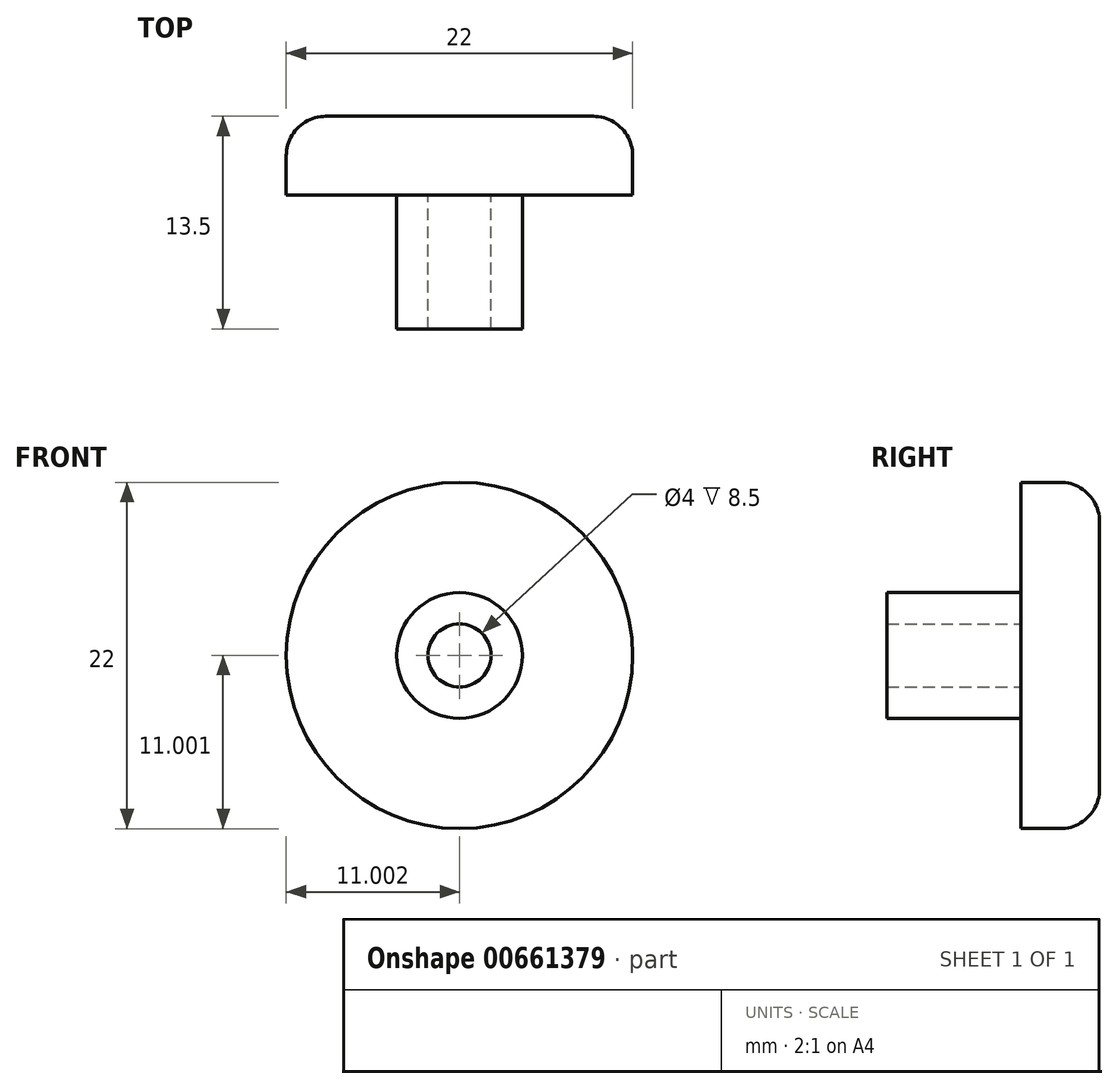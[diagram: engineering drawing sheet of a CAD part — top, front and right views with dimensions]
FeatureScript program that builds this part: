
annotation { "Feature Type Name" : "Feature", "Feature Type Description" : "" }
export const myFeature = defineFeature(function(context is Context, id is Id, definition is map)
    precondition{}
    {
        {
            var Q0;
            Q0=qCreatedBy(makeId("Front.planeOp"),FACE);
            var sketch = newSketch(context, id + "F0", { "sketchPlane" : qUnion([Q0])});
            skCircle(sketch, "E0", {"center": v(39.71, 36.2) * mm, "radius": 11 * mm});
            skCircle(sketch, "E1", {"center": v(39.71, 36.2) * mm, "radius": 4 * mm});
            skCircle(sketch, "E2", {"center": v(39.71, 36.2) * mm, "radius": 2 * mm});
            skSolve(sketch);
        }
        {
            var Q0;
            Q0=makeQuery(id+"F0.imprint","IMPRINT",FACE,{"disambiguationData":[TD([[makeQuery(id+"F0.imprint","IMPRINT",EDGE,{"derivedFrom":sQuery(id+"F0.wireOp",EDGE,"E1")}),1.0]])]});
            extrude(context, id + "F1", {"entities" : qUnion([Q0]), "depth" : 13.5 * mm, "offsetDistance" : 25 * mm});
        }
        {
            var Q0;
            Q0=makeQuery(id+"F0.imprint","IMPRINT",FACE,{"disambiguationData":[TD([[makeQuery(id+"F0.imprint","IMPRINT",EDGE,{"derivedFrom":sQuery(id+"F0.wireOp",EDGE,"E0")}),1.0]])]});
            extrude(context, id + "F2", {"entities" : qUnion([Q0]), "operationType" : NewBodyOperationType.ADD, "depth" : 5 * mm, "offsetDistance" : 25 * mm});
        }
        {
            var Q0;
            Q0=makeQuery(id+"F2.opExtrude","CAP_EDGE",EDGE,{"disambiguationData":[OSD([sQuery(id+"F0.wireOp",EDGE,"E0")])],"isStart":true});
            fillet(context, id + "F3", {"entities" : qUnion([Q0]), "radius" : 2.5 * mm, "tangentPropagation" : true, "allowEdgeOverflow" : false});
        }
        {
            var Q0;
            Q0=makeQuery(id+"F0.imprint","IMPRINT",FACE,{"disambiguationData":[TD([[makeQuery(id+"F0.imprint","IMPRINT",EDGE,{"derivedFrom":sQuery(id+"F0.wireOp",EDGE,"E2")}),1.0]])]});
            extrude(context, id + "F4", {"entities" : qUnion([Q0]), "operationType" : NewBodyOperationType.ADD, "depth" : 5 * mm, "offsetDistance" : 25 * mm});
        }
    });
